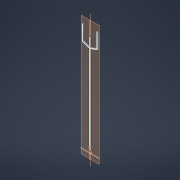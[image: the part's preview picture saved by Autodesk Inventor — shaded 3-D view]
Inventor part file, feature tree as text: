
AUTODESK INVENTOR PART (.ipt)
format: ipt  version: 2021 (Build 250183000, 183)  size: 134,656 bytes
history: native  units: mm
features: extrude x2, sketch x2, mirror x1, plane x1
ambient origin geometry x8: Origin, YZ Plane, XZ Plane, XY Plane, X Axis, Y Axis, Z Axis, Center Point
bodies: Solid1 (feature_tree)
feature tree (6):
  extrude  "Extrusion1"  Depth=4.0mm
  mirror  "Mirror1"
  plane  "Work Plane1"
  extrude  "Extrusion2"  Depth=2.0mm TaperAngle=0.0deg
  sketch  "Sketch1"  dims[d6=15.0mm d7=4.0mm]
  sketch  "Sketch3"  dims[d12=4.0mm d16=2.0mm d17=0.0mm d19=2.0mm d20=270.0mm d22=135.0deg d23=2.0mm d24=12.217305mm d26=2.0mm d27=20.0mm d28=135.0deg d31=35.0mm d32=20.0mm d33=0.0mm d34=0.0mm]
